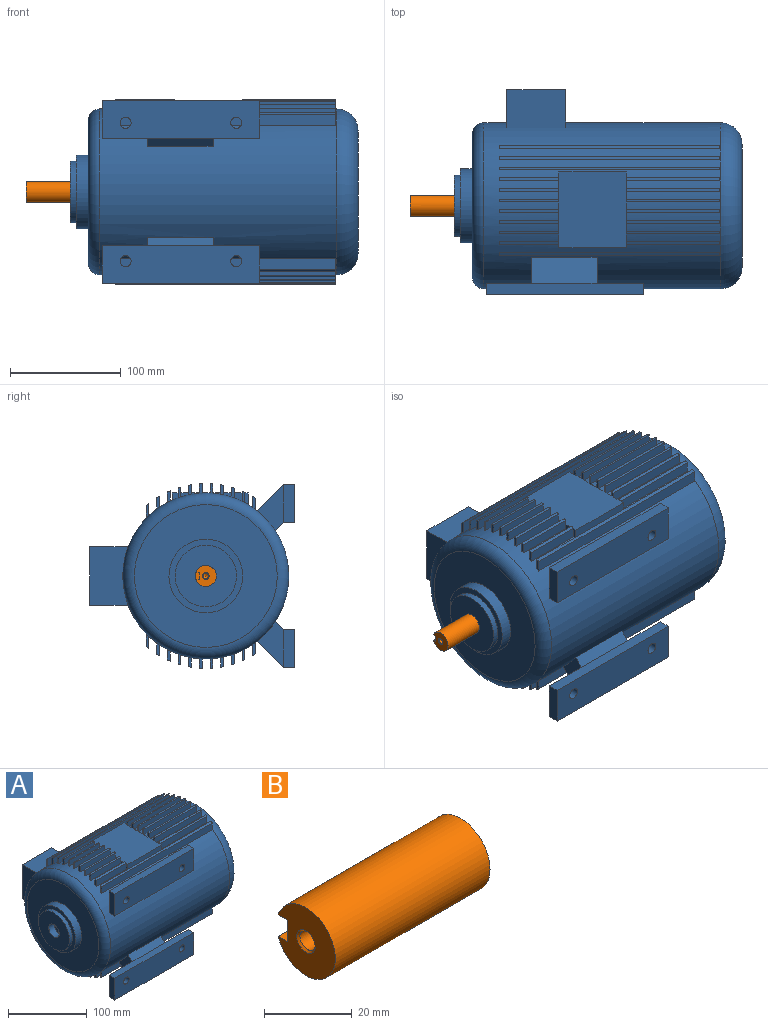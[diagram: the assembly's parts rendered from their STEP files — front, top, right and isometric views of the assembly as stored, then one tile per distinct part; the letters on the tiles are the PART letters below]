
ASSEMBLY  parts=2 mates=1
PART A: 208 faces, bbox 260x186.2x166.9 mm
  f0: plane 53.04x34.85mm, normal (1,0,0), area 1675.7mm2, adj f42,f189,f191,f207
  f1: plane 60.84x10.47mm, normal (0,-1,0), area 636.9mm2, adj f3,f20,f42,f206
  f2: plane 60.84x6.45mm, normal (0,1,0), area 392.2mm2, adj f11,f12,f42,f206
  f3: plane 10.47x3.05mm, normal (-1,0,0), area 29.3mm2, adj f1,f21,f42,f206
  f4: plane 7.53x7.23mm, normal (-1,0,0), area 42.9mm2, adj f22,f23,f42,f206
  f5: plane 7.23x3.65mm, normal (-1,0,0), area 18.9mm2, adj f24,f25,f42,f206
  f6: plane 7.23x1.22mm, normal (-1,0,0), area 4.9mm2, adj f26,f27,f42,f206
  f7: plane 3.85x0.1mm, normal (-1,0,0), area 0.1mm2, adj f28,f42,f206
  f8: plane 3.37x0.08mm, normal (-1,0,0), area 0.1mm2, adj f30,f42,f206
  f9: plane 7.23x1.14mm, normal (-1,0,0), area 4.5mm2, adj f29,f32,f42,f206
  f10: plane 7.23x3.5mm, normal (-1,0,0), area 18mm2, adj f31,f34,f42,f206
  f11: plane 6.45x5.37mm, normal (-1,0,0), area 28.7mm2, adj f2,f33,f42,f206
  f12: plane 6.45x5.37mm, normal (1,0,0), area 28.7mm2, adj f2,f42,f100,f206
  f13: plane 7.23x3.5mm, normal (1,0,0), area 18mm2, adj f42,f92,f102,f206
  f14: plane 7.23x1.14mm, normal (1,0,0), area 4.5mm2, adj f42,f84,f94,f206
  f15: plane 3.37x0.08mm, normal (1,0,0), area 0.1mm2, adj f42,f86,f206
  f16: plane 3.85x0.1mm, normal (1,0,0), area 0.1mm2, adj f42,f81,f206
  f17: plane 7.23x1.22mm, normal (1,0,0), area 4.9mm2, adj f42,f73,f79,f206
  f18: plane 7.23x3.65mm, normal (1,0,0), area 18.9mm2, adj f42,f65,f71,f206
  f19: plane 7.53x7.23mm, normal (1,0,0), area 42.9mm2, adj f42,f57,f63,f206
  f20: plane 10.47x3.05mm, normal (1,0,0), area 29.3mm2, adj f1,f42,f55,f206
  f21: plane 53.96x9.49mm, normal (0,-1,0), area 512mm2, adj f3,f41,f42,f56,f198
  f22: plane 53.96x9.34mm, normal (0,1,0), area 503.8mm2, adj f4,f41,f42,f56,f198
  f23: plane 53.96x8.98mm, normal (0,-1,0), area 484.5mm2, adj f4,f40,f42,f64,f197
  f24: plane 53.96x8.89mm, normal (0,1,0), area 479.5mm2, adj f5,f40,f42,f64,f197
  f25: plane 53.96x8.68mm, normal (0,-1,0), area 468.2mm2, adj f5,f39,f42,f72,f196
  f26: plane 53.96x8.63mm, normal (0,1,0), area 465.4mm2, adj f6,f39,f42,f72,f196
  f27: plane 53.96x8.53mm, normal (0,-1,0), area 460.1mm2, adj f6,f38,f42,f80,f195
  f28: plane 53.96x8.51mm, normal (0,1,0), area 459.2mm2, adj f7,f38,f42,f80,f195
  f29: plane 53.96x8.52mm, normal (0,1,0), area 459.8mm2, adj f9,f37,f42,f85,f194
  f30: plane 53.96x8.51mm, normal (0,-1,0), area 459mm2, adj f8,f37,f42,f85,f194
  f31: plane 53.96x8.67mm, normal (0,1,0), area 467.6mm2, adj f10,f36,f42,f93,f193
  f32: plane 53.96x8.62mm, normal (0,-1,0), area 464.9mm2, adj f9,f36,f42,f93,f193
  f33: plane 53.96x8.96mm, normal (0,1,0), area 483.5mm2, adj f11,f35,f42,f101,f192
  f34: plane 53.96x8.87mm, normal (0,-1,0), area 478.6mm2, adj f10,f35,f42,f101,f192
  f35: cylinder r=83.5mm len=53.96mm, axis (1,0,0), area 135.6mm2, adj f33,f34,f101,f192
  f36: cylinder r=83.5mm len=53.96mm, axis (1,0,0), area 131.9mm2, adj f31,f32,f93,f193
  f37: cylinder r=83.5mm len=53.96mm, axis (1,0,0), area 130.2mm2, adj f29,f30,f85,f194
  f38: cylinder r=83.5mm len=53.96mm, axis (1,0,0), area 130.2mm2, adj f27,f28,f80,f195
  f39: cylinder r=83.5mm len=53.96mm, axis (1,0,0), area 132mm2, adj f25,f26,f72,f196
  f40: cylinder r=83.5mm len=53.96mm, axis (1,0,0), area 135.9mm2, adj f23,f24,f64,f197
  f41: cylinder r=83.5mm len=53.96mm, axis (1,0,0), area 142.3mm2, adj f21,f22,f56,f198
  f42: cylinder r=75mm len=213.81mm, axis (-1,0,0), area 79991.6mm2, adj f0,f1,f2,f3,f4,f5,f6,f7
  f43: plane 11.79x2.41mm, normal (1,0,0), area 24.5mm2, adj f42,f44,f46,f162
  f44: plane 199.16x10.07mm, normal (0,1,0), area 2005.2mm2, adj f42,f43,f45,f162
  f45: plane 11.79x2.41mm, normal (-1,0,0), area 24.5mm2, adj f42,f44,f46,f162
  f46: plane 199.16x10.31mm, normal (0,-1,0), area 2054.3mm2, adj f42,f43,f45,f162
  f47: plane 199.16x10.31mm, normal (0,-1,0), area 2054.3mm2, adj f42,f48,f50,f161
  f48: plane 11.79x2.41mm, normal (-1,0,0), area 24.5mm2, adj f42,f47,f49,f161
  f49: plane 199.16x10.07mm, normal (0,1,0), area 2005.2mm2, adj f42,f48,f50,f161
  f50: plane 11.79x2.41mm, normal (1,0,0), area 24.5mm2, adj f42,f47,f49,f161
  f51: plane 10.56x2.41mm, normal (1,0,0), area 22.7mm2, adj f42,f52,f54,f160
  f52: plane 199.16x9.34mm, normal (0,1,0), area 1859.8mm2, adj f42,f51,f53,f160
  f53: plane 10.56x2.41mm, normal (-1,0,0), area 22.7mm2, adj f42,f52,f54,f160
  f54: plane 199.16x9.49mm, normal (0,-1,0), area 1889.8mm2, adj f42,f51,f53,f160
  f55: plane 84.37x9.49mm, normal (0,-1,0), area 800.5mm2, adj f20,f42,f58,f159,f199
  f56: plane 10.56x2.41mm, normal (-1,0,0), area 22.7mm2, adj f21,f22,f41,f42
  f57: plane 84.37x9.34mm, normal (0,1,0), area 787.8mm2, adj f19,f42,f58,f159,f199
  f58: plane 10.56x2.41mm, normal (1,0,0), area 22.7mm2, adj f42,f55,f57,f159
  f59: plane 9.71x2.41mm, normal (1,0,0), area 21.5mm2, adj f42,f60,f62,f158
  f60: plane 199.16x8.89mm, normal (0,1,0), area 1770.1mm2, adj f42,f59,f61,f158
  f61: plane 9.71x2.41mm, normal (-1,0,0), area 21.5mm2, adj f42,f60,f62,f158
  f62: plane 199.16x8.98mm, normal (0,-1,0), area 1788.5mm2, adj f42,f59,f61,f158
  f63: plane 84.37x8.98mm, normal (0,-1,0), area 757.6mm2, adj f19,f42,f66,f157,f200
  f64: plane 9.71x2.41mm, normal (-1,0,0), area 21.5mm2, adj f23,f24,f40,f42
  f65: plane 84.37x8.89mm, normal (0,1,0), area 749.8mm2, adj f18,f42,f66,f157,f200
  f66: plane 9.71x2.41mm, normal (1,0,0), area 21.5mm2, adj f42,f63,f65,f157
  f67: plane 9.11x2.41mm, normal (1,0,0), area 20.8mm2, adj f42,f68,f70,f156
  f68: plane 199.16x8.63mm, normal (0,1,0), area 1718mm2, adj f42,f67,f69,f156
  f69: plane 9.11x2.41mm, normal (-1,0,0), area 20.8mm2, adj f42,f68,f70,f156
  f70: plane 199.16x8.68mm, normal (0,-1,0), area 1728.1mm2, adj f42,f67,f69,f156
  f71: plane 84.37x8.68mm, normal (0,-1,0), area 732mm2, adj f18,f42,f74,f155,f201
  f72: plane 9.11x2.41mm, normal (-1,0,0), area 20.8mm2, adj f25,f26,f39,f42
  f73: plane 84.37x8.63mm, normal (0,1,0), area 727.8mm2, adj f17,f42,f74,f155,f201
  f74: plane 9.11x2.41mm, normal (1,0,0), area 20.8mm2, adj f42,f71,f73,f155
  f75: plane 8.67x2.41mm, normal (1,0,0), area 20.5mm2, adj f42,f76,f78,f154
  f76: plane 199.16x8.51mm, normal (0,1,0), area 1694.9mm2, adj f42,f75,f77,f154
  f77: plane 8.67x2.41mm, normal (-1,0,0), area 20.5mm2, adj f42,f76,f78,f154
  f78: plane 199.16x8.53mm, normal (0,-1,0), area 1698.2mm2, adj f42,f75,f77,f154
  f79: plane 84.37x8.53mm, normal (0,-1,0), area 719.4mm2, adj f17,f42,f82,f153,f202
  f80: plane 8.67x2.41mm, normal (-1,0,0), area 20.5mm2, adj f27,f28,f38,f42
  f81: plane 84.37x8.51mm, normal (0,1,0), area 718mm2, adj f16,f42,f82,f153,f202
  f82: plane 8.67x2.41mm, normal (1,0,0), area 20.5mm2, adj f42,f79,f81,f153
  f83: plane 8.66x2.41mm, normal (1,0,0), area 20.5mm2, adj f42,f84,f86,f152
  f84: plane 84.37x8.52mm, normal (0,1,0), area 719mm2, adj f14,f42,f83,f152,f203
  f85: plane 8.66x2.41mm, normal (-1,0,0), area 20.5mm2, adj f29,f30,f37,f42
  f86: plane 84.37x8.51mm, normal (0,-1,0), area 717.8mm2, adj f15,f42,f83,f152,f203
  f87: plane 199.16x8.51mm, normal (0,-1,0), area 1694.4mm2, adj f42,f88,f90,f151
  f88: plane 8.66x2.41mm, normal (-1,0,0), area 20.5mm2, adj f42,f87,f89,f151
  f89: plane 199.16x8.52mm, normal (0,1,0), area 1697.4mm2, adj f42,f88,f90,f151
  f90: plane 8.66x2.41mm, normal (1,0,0), area 20.5mm2, adj f42,f87,f89,f151
  f91: plane 9.08x2.41mm, normal (1,0,0), area 20.8mm2, adj f42,f92,f94,f150
  f92: plane 84.37x8.67mm, normal (0,1,0), area 731.1mm2, adj f13,f42,f91,f150,f204
  f93: plane 9.08x2.41mm, normal (-1,0,0), area 20.8mm2, adj f31,f32,f36,f42
  f94: plane 84.37x8.62mm, normal (0,-1,0), area 727mm2, adj f14,f42,f91,f150,f204
  f95: plane 199.16x8.62mm, normal (0,-1,0), area 1716.2mm2, adj f42,f96,f98,f149
  f96: plane 9.08x2.41mm, normal (-1,0,0), area 20.8mm2, adj f42,f95,f97,f149
  f97: plane 199.16x8.67mm, normal (0,1,0), area 1725.9mm2, adj f42,f96,f98,f149
  f98: plane 9.08x2.41mm, normal (1,0,0), area 20.8mm2, adj f42,f95,f97,f149
  f99: plane 9.68x2.41mm, normal (1,0,0), area 21.5mm2, adj f42,f100,f102,f148
  f100: plane 84.37x8.96mm, normal (0,1,0), area 756mm2, adj f12,f42,f99,f148,f205
  f101: plane 9.68x2.41mm, normal (-1,0,0), area 21.5mm2, adj f33,f34,f35,f42
  f102: plane 84.37x8.87mm, normal (0,-1,0), area 748.4mm2, adj f13,f42,f99,f148,f205
  f103: plane 199.16x8.87mm, normal (0,-1,0), area 1766.7mm2, adj f42,f104,f106,f147
  f104: plane 9.68x2.41mm, normal (-1,0,0), area 21.5mm2, adj f42,f103,f105,f147
  f105: plane 199.16x8.96mm, normal (0,1,0), area 1784.7mm2, adj f42,f104,f106,f147
  f106: plane 9.68x2.41mm, normal (1,0,0), area 21.5mm2, adj f42,f103,f105,f147
  f107: plane 10.51x2.41mm, normal (1,0,0), area 22.6mm2, adj f42,f108,f110,f146
  f108: plane 199.16x9.46mm, normal (0,1,0), area 1883.6mm2, adj f42,f107,f109,f146
  f109: plane 10.51x2.41mm, normal (-1,0,0), area 22.6mm2, adj f42,f108,f110,f146
  f110: plane 199.16x9.31mm, normal (0,-1,0), area 1854.2mm2, adj f42,f107,f109,f146
  f111: plane 199.16x9.31mm, normal (0,-1,0), area 1854.2mm2, adj f42,f112,f114,f145
  f112: plane 10.51x2.41mm, normal (-1,0,0), area 22.6mm2, adj f42,f111,f113,f145
  f113: plane 199.16x9.46mm, normal (0,1,0), area 1883.6mm2, adj f42,f112,f114,f145
  f114: plane 10.51x2.41mm, normal (1,0,0), area 22.6mm2, adj f42,f111,f113,f145
  f115: plane 11.72x2.41mm, normal (1,0,0), area 24.4mm2, adj f42,f116,f118,f144
  f116: plane 199.16x10.26mm, normal (0,1,0), area 2044mm2, adj f42,f115,f117,f144
  f117: plane 11.72x2.41mm, normal (-1,0,0), area 24.4mm2, adj f42,f116,f118,f144
  f118: plane 199.16x10.02mm, normal (0,-1,0), area 1996.2mm2, adj f42,f115,f117,f144
  f119: plane 199.16x10.02mm, normal (0,-1,0), area 1996.2mm2, adj f42,f120,f122,f143
  f120: plane 11.72x2.41mm, normal (-1,0,0), area 24.4mm2, adj f42,f119,f121,f143
  f121: plane 199.16x10.26mm, normal (0,1,0), area 2044mm2, adj f42,f120,f122,f143
  f122: plane 11.72x2.41mm, normal (1,0,0), area 24.4mm2, adj f42,f119,f121,f143
  f123: plane 13.6x2.41mm, normal (1,0,0), area 27.5mm2, adj f42,f124,f126,f142
  f124: plane 199.16x11.63mm, normal (0,1,0), area 2316.6mm2, adj f42,f123,f125,f142
  f125: plane 13.6x2.41mm, normal (-1,0,0), area 27.5mm2, adj f42,f124,f126,f142
  f126: plane 199.16x11.21mm, normal (0,-1,0), area 2232.8mm2, adj f42,f123,f125,f142
  f127: plane 199.16x11.21mm, normal (0,-1,0), area 2232.8mm2, adj f42,f128,f130,f141
  f128: plane 13.6x2.41mm, normal (-1,0,0), area 27.5mm2, adj f42,f127,f129,f141
  f129: plane 199.16x11.63mm, normal (0,1,0), area 2316.6mm2, adj f42,f128,f130,f141
  f130: plane 13.6x2.41mm, normal (1,0,0), area 27.5mm2, adj f42,f127,f129,f141
  f131: plane 111.11x111.11mm, normal (1,0,0), area 9696.3mm2, adj f132
  f132: torus R=55.56mm, axis (-1,0,0), area 13037.2mm2, adj f42,f131
  f133: torus R=64.5mm, axis (-1,0,0), area 7376.9mm2, adj f42,f134
  f134: plane 129x129mm, normal (-1,0,0), area 9579.2mm2, adj f133,f135
  f135: cylinder r=33.33mm len=66.67mm, axis (-1,0,0), area 2268.9mm2, adj f134,f136
  f136: plane 66.67x66.67mm, normal (-1,0,0), area 1066.6mm2, adj f135,f137
  f137: cylinder r=27.78mm len=55.56mm, axis (-1,0,0), area 945.4mm2, adj f136,f138
  f138: plane 55.56x55.56mm, normal (-1,0,0), area 2140.5mm2, adj f137,f139
  f139: cylinder r=9.5mm len=19mm, axis (1,0,0), area 596.9mm2, adj f138,f140
  f140: plane 19x19mm, normal (-1,0,0), area 283.5mm2, adj f139
  f141: cylinder r=83.5mm len=199.16mm, axis (1,0,0), area 618.9mm2, adj f127,f128,f129,f130
  f142: cylinder r=83.5mm len=199.16mm, axis (1,0,0), area 618.9mm2, adj f123,f124,f125,f126
  f143: cylinder r=83.5mm len=199.16mm, axis (1,0,0), area 560.2mm2, adj f119,f120,f121,f122
  f144: cylinder r=83.5mm len=199.16mm, axis (1,0,0), area 560.2mm2, adj f115,f116,f117,f118
  f145: cylinder r=83.5mm len=199.16mm, axis (1,0,0), area 523.7mm2, adj f111,f112,f113,f114
  f146: cylinder r=83.5mm len=199.16mm, axis (1,0,0), area 523.7mm2, adj f107,f108,f109,f110
  f147: cylinder r=83.5mm len=199.16mm, axis (1,0,0), area 500.6mm2, adj f103,f104,f105,f106
  f148: cylinder r=83.5mm len=84.37mm, axis (1,0,0), area 212mm2, adj f99,f100,f102,f205
  f149: cylinder r=83.5mm len=199.16mm, axis (1,0,0), area 486.8mm2, adj f95,f96,f97,f98
  f150: cylinder r=83.5mm len=84.37mm, axis (1,0,0), area 206.2mm2, adj f91,f92,f94,f204
  f151: cylinder r=83.5mm len=199.16mm, axis (1,0,0), area 480.4mm2, adj f87,f88,f89,f90
  f152: cylinder r=83.5mm len=84.37mm, axis (1,0,0), area 203.5mm2, adj f83,f84,f86,f203
  f153: cylinder r=83.5mm len=84.37mm, axis (1,0,0), area 203.6mm2, adj f79,f81,f82,f202
  f154: cylinder r=83.5mm len=199.16mm, axis (1,0,0), area 480.6mm2, adj f75,f76,f77,f78
  f155: cylinder r=83.5mm len=84.37mm, axis (1,0,0), area 206.4mm2, adj f71,f73,f74,f201
  f156: cylinder r=83.5mm len=199.16mm, axis (1,0,0), area 487.3mm2, adj f67,f68,f69,f70
  f157: cylinder r=83.5mm len=84.37mm, axis (1,0,0), area 212.4mm2, adj f63,f65,f66,f200
  f158: cylinder r=83.5mm len=199.16mm, axis (1,0,0), area 501.5mm2, adj f59,f60,f61,f62
  f159: cylinder r=83.5mm len=84.37mm, axis (1,0,0), area 222.4mm2, adj f55,f57,f58,f199
  f160: cylinder r=83.5mm len=199.16mm, axis (1,0,0), area 525.1mm2, adj f51,f52,f53,f54
  f161: cylinder r=83.5mm len=199.16mm, axis (1,0,0), area 562.5mm2, adj f47,f48,f49,f50
  f162: cylinder r=83.5mm len=199.16mm, axis (1,0,0), area 562.5mm2, adj f43,f44,f45,f46
  f163: plane 142x34mm, normal (0,-1,0), area 4670.9mm2, adj f164,f165,f166,f167,f168,f169
  f164: plane 34x10mm, normal (-1,0,0), area 340mm2, adj f163,f168,f169,f170
  f165: cylinder r=5mm len=10mm, axis (0,-1,0), area 314.2mm2, adj f163,f170
  f166: plane 34x10mm, normal (1,0,0), area 340mm2, adj f163,f168,f169,f171
  f167: cylinder r=5mm len=10mm, axis (0,-1,0), area 314.2mm2, adj f163,f171
  f168: plane 142x10mm, normal (0,0,-1), area 1420mm2, adj f163,f164,f166,f170,f171,f175
  f169: plane 142x10mm, normal (0,0,1), area 1420mm2, adj f163,f164,f166,f170,f171,f174
  f170: plane 41x34mm, normal (0,1,0), area 1315.5mm2, adj f164,f165,f168,f169,f172
  f171: plane 42x34mm, normal (0,1,0), area 1349.5mm2, adj f166,f167,f168,f169,f173
  f172: plane 41.32x23.59mm, normal (-1,0,0), area 509.8mm2, adj f42,f170,f174,f175
  f173: plane 41.32x23.59mm, normal (1,0,0), area 509.8mm2, adj f42,f171,f174,f175
  f174: plane 59x23.59mm, normal (0,0.71,0.71), area 1968mm2, adj f42,f169,f172,f173
  f175: plane 59x7.32mm, normal (0,-0.71,-0.71), area 610.6mm2, adj f42,f168,f172,f173
  f176: plane 59x7.32mm, normal (0,-0.71,0.71), area 610.6mm2, adj f42,f178,f179,f180
  f177: plane 59x23.59mm, normal (0,0.71,-0.71), area 1968mm2, adj f42,f178,f179,f182
  f178: plane 41.32x23.59mm, normal (-1,0,0), area 509.8mm2, adj f42,f176,f177,f185
  f179: plane 41.32x23.59mm, normal (1,0,0), area 509.8mm2, adj f42,f176,f177,f186
  f180: plane 142x10mm, normal (0,0,1), area 1420mm2, adj f176,f181,f183,f184,f185,f186
  f181: plane 142x34mm, normal (0,-1,0), area 4670.9mm2, adj f180,f182,f183,f184,f187,f188
  f182: plane 142x10mm, normal (0,0,-1), area 1420mm2, adj f177,f181,f183,f184,f185,f186
  f183: plane 34x10mm, normal (1,0,0), area 340mm2, adj f180,f181,f182,f186
  f184: plane 34x10mm, normal (-1,0,0), area 340mm2, adj f180,f181,f182,f185
  f185: plane 41x34mm, normal (0,1,0), area 1315.5mm2, adj f178,f180,f182,f184,f187
  f186: plane 42x34mm, normal (0,1,0), area 1349.5mm2, adj f179,f180,f182,f183,f188
  f187: cylinder r=5mm len=10mm, axis (0,-1,0), area 314.2mm2, adj f181,f185
  f188: cylinder r=5mm len=10mm, axis (0,-1,0), area 314.2mm2, adj f181,f186
  f189: plane 53.04x34.85mm, normal (0,0,1), area 1848.2mm2, adj f0,f42,f190,f207
  f190: plane 53.04x34.85mm, normal (-1,0,0), area 1675.7mm2, adj f42,f189,f191,f207
  f191: plane 53.04x34.85mm, normal (0,0,-1), area 1848.2mm2, adj f0,f42,f190,f207
  f192: plane 5.37x2.41mm, normal (1,0,0), area 12.1mm2, adj f33,f34,f35,f206
  f193: plane 7.48x2.41mm, normal (1,0,0), area 17.5mm2, adj f31,f32,f36,f206
  f194: plane 8.43x2.41mm, normal (1,0,0), area 20.2mm2, adj f29,f30,f37,f206
  f195: plane 8.41x2.41mm, normal (1,0,0), area 20.1mm2, adj f27,f28,f38,f206
  f196: plane 7.4x2.41mm, normal (1,0,0), area 17.3mm2, adj f25,f26,f39,f206
  f197: plane 5.23x2.41mm, normal (1,0,0), area 11.7mm2, adj f23,f24,f40,f206
  f198: plane 2.41x1.81mm, normal (1,0,0), area 3.1mm2, adj f21,f22,f41,f206
  f199: plane 2.41x1.81mm, normal (-1,0,0), area 3.1mm2, adj f55,f57,f159,f206
  f200: plane 5.23x2.41mm, normal (-1,0,0), area 11.7mm2, adj f63,f65,f157,f206
  f201: plane 7.4x2.41mm, normal (-1,0,0), area 17.3mm2, adj f71,f73,f155,f206
  f202: plane 8.41x2.41mm, normal (-1,0,0), area 20.1mm2, adj f79,f81,f153,f206
  f203: plane 8.43x2.41mm, normal (-1,0,0), area 20.2mm2, adj f84,f86,f152,f206
  f204: plane 7.48x2.41mm, normal (-1,0,0), area 17.5mm2, adj f92,f94,f150,f206
  f205: plane 5.37x2.41mm, normal (-1,0,0), area 12.1mm2, adj f100,f102,f148,f206
  f206: plane 68.64x60.84mm, normal (0,0,1), area 4176.1mm2, adj f1,f2,f3,f4,f5,f6,f7,f8
  f207: plane 53.04x53.04mm, normal (0,1,0), area 2813.2mm2, adj f0,f189,f190,f191
PART B: 13 faces, bbox 50x19x19 mm
  f0: plane 19x18.51mm, normal (-1,0,0), area 235.2mm2, adj f2,f3,f4,f5,f12
  f1: plane 19x19mm, normal (1,0,0), area 283.5mm2, adj f2
  f2: cylinder r=9.5mm len=50mm, axis (1,0,0), area 2746.4mm2, adj f0,f1,f3,f5,f6
  f3: plane 39x3.01mm, normal (0,0,-1), area 117.5mm2, adj f0,f2,f4,f6
  f4: plane 39x6mm, normal (0,1,0), area 234mm2, adj f0,f3,f5,f6
  f5: plane 39x3.01mm, normal (0,0,1), area 117.5mm2, adj f0,f2,f4,f6
  f6: plane 6x3.5mm, normal (-1,0,0), area 20mm2, adj f2,f3,f4,f5
  f7: cone r=0mm half-angle=60deg, axis (-1,0,0), area 21.9mm2, adj f8
  f8: cylinder r=2.46mm len=4.92mm, axis (-1,0,0), area 41.1mm2, adj f7,f9
  f9: cone r=2.46mm half-angle=45deg, axis (-1,0,0), area 13.1mm2, adj f8,f10
  f10: plane 6x6mm, normal (1,0,0), area 9.3mm2, adj f9,f11
  f11: cylinder r=2.46mm len=15.46mm, axis (-1,0,0), area 238.8mm2, adj f10,f12
  f12: cone r=2.46mm half-angle=45deg, axis (-1,0,0), area 13.1mm2, adj f0,f11
PLACE A at identity
PLACE B at identity
MATE fastened B.f2 <-> A.f35  axis (1,0,0) through (10,0,0)mm
